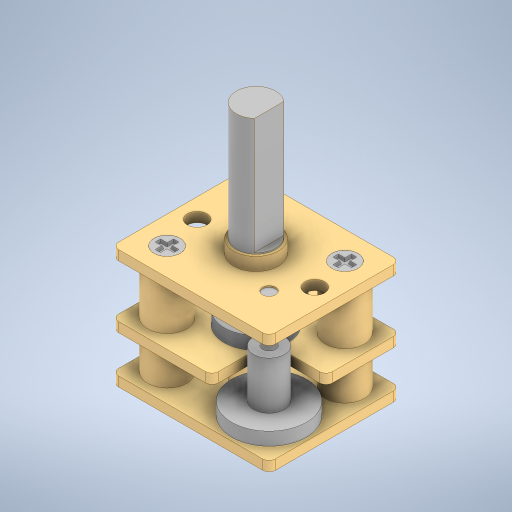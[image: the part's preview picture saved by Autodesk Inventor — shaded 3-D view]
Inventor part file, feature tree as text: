
AUTODESK INVENTOR PART (.ipt)
format: ipt  version: 2023 (Build 270158000, 158)  size: 488,960 bytes
history: native  units: in
note: dims shown in document units (in); Inventor stores cm internally (conversion verified against a paired STEP export)
features: extrude x2, sketch x2, other x1
ambient origin geometry x8: Origin, YZ Plane, XZ Plane, XY Plane, X Axis, Y Axis, Z Axis, Center Point
bodies: Solid1 (feature_tree), Solid2 (feature_tree), Solid3 (feature_tree), Solid4 (feature_tree), Solid5 (feature_tree), Solid6 (feature_tree), Solid7 (feature_tree), Solid8 (feature_tree), Solid9 (feature_tree), Solid10 (feature_tree), Solid11 (feature_tree), Solid12 (feature_tree), Solid13 (feature_tree), Solid14 (feature_tree), Solid16 (feature_tree), Body1 (feature_tree), Body3 (feature_tree), Body4 (feature_tree), Body5 (feature_tree), Body6 (feature_tree), Body7 (feature_tree), Body8 (feature_tree), Body9 (feature_tree), Body10 (feature_tree), Body12 (feature_tree), Body14 (feature_tree), Body15 (feature_tree), Body17 (feature_tree), Body18 (feature_tree)
feature tree (5):
  extrude  "Extrusion1"  Depth=0.3543in TaperAngle=0.0deg
  extrude  "Extrusion2"  Depth=0.3504in TaperAngle=0.0deg
  sketch  "Sketch2"  dims[d0=0.1181in d1=0.3543in d2=0.0in]
  sketch  "Sketch3"  dims[d3=0.0984in d4=0.3504in d5=0.0in]
  other  "Body12:1"
